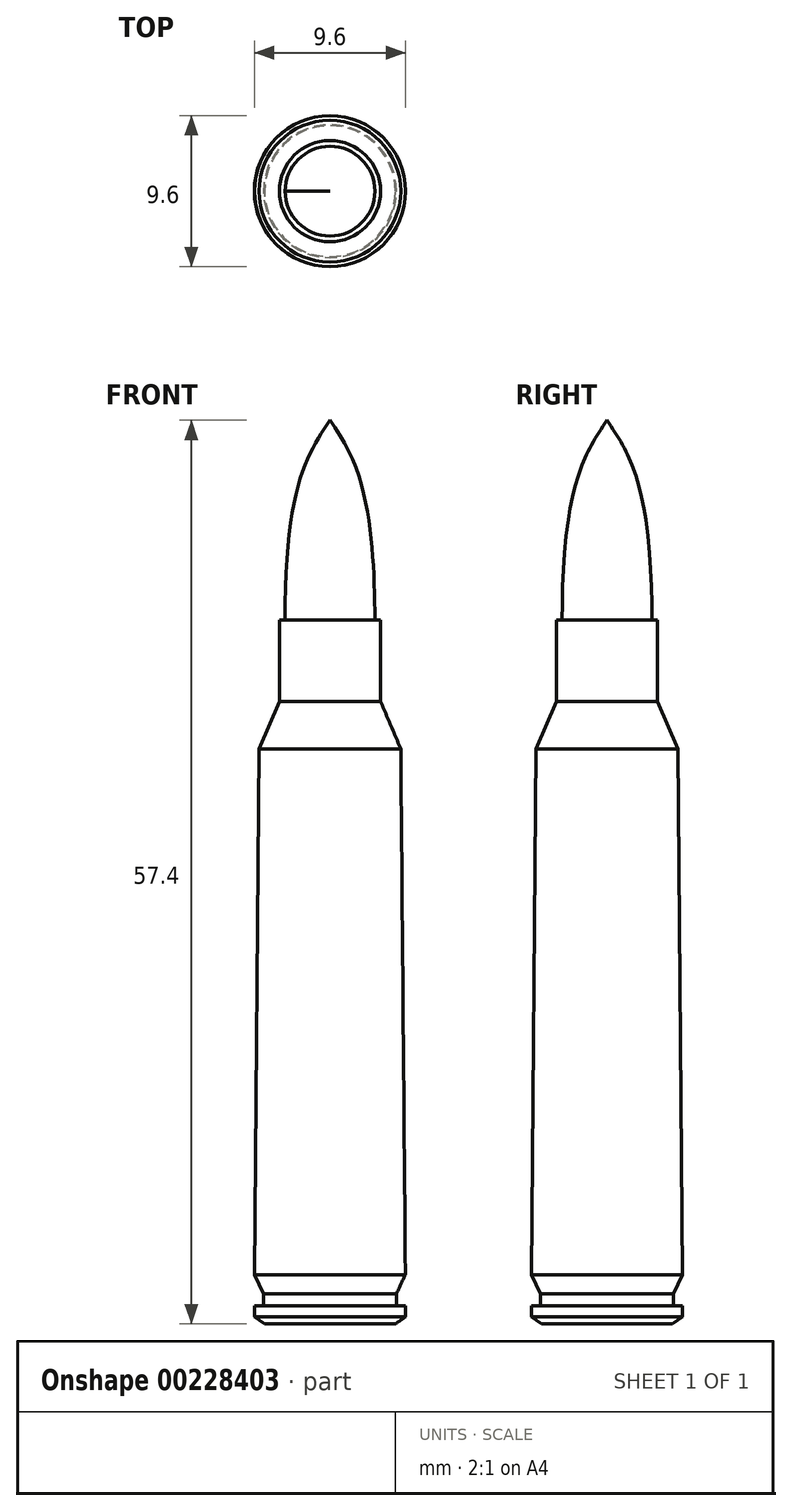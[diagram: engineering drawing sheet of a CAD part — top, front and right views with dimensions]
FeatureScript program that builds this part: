
annotation { "Feature Type Name" : "Feature", "Feature Type Description" : "" }
export const myFeature = defineFeature(function(context is Context, id is Id, definition is map)
    precondition{}
    {
        {
            var Q0;
            Q0=qCreatedBy(makeId("Top.planeOp"),FACE);
            var sketch = newSketch(context, id + "F0", { "sketchPlane" : qUnion([Q0])});
            skCircle(sketch, "E0", {"center": v(0, 0) * mm, "radius": 2.85 * mm});
            skCircle(sketch, "E1", {"center": v(0, 0) * mm, "radius": 3.21 * mm});
            skSolve(sketch);
        }
        {
            var Q0;
            Q0=qCreatedBy(makeId("Top.planeOp"),FACE);
            cPlane(context, id + "F1", {"entities" : qUnion([Q0]), "cplaneType" : CPlaneType.OFFSET, "offset" : 44.7 * mm, "oppositeDirection" : true, "width" : 150 * mm, "height" : 150 * mm});
        }
        {
            var Q0;
            Q0=qCreatedBy(id+"F1.planeOp",FACE);
            cPlane(context, id + "F2", {"entities" : qUnion([Q0]), "cplaneType" : CPlaneType.OFFSET, "offset" : 57.4 * mm, "width" : 150 * mm, "height" : 150 * mm});
        }
        {
            var Q0;
            Q0=qCreatedBy(id+"F2.planeOp",FACE);
            var sketch = newSketch(context, id + "F3", { "sketchPlane" : qUnion([Q0])});
            skPoint(sketch, "E2", {"position": v(0, 0) * mm});
            skSolve(sketch);
        }
        {
            var Q0;
            Q0=makeQuery(id+"F0.imprint","IMPRINT",FACE,{"disambiguationData":[TD([[makeQuery(id+"F0.imprint","IMPRINT",EDGE,{"derivedFrom":sQuery(id+"F0.wireOp",EDGE,"E0")}),1.0]])]});
            var Q1;
            Q1=sQuery(id+"F3.wireOp",VERTEX,"E2");
            loft(context, id + "F4", {"startCondition" : LoftEndDerivativeType.NORMAL_TO_PROFILE, "startMagnitude" : 2, "sheetProfilesArray" : [{ "sheetProfileEntities" : qUnion([Q0]) }, { "sheetProfileEntities" : qUnion([Q1]) }]});
        }
        {
            var Q0;
            Q0=qCreatedBy(makeId("Top.planeOp"),FACE);
            var sketch = newSketch(context, id + "F5", { "sketchPlane" : qUnion([Q0])});
            skCircle(sketch, "E3", {"center": v(0, 0) * mm, "radius": 3.21 * mm});
            skSolve(sketch);
        }
        {
            var Q0;
            Q0=qCreatedBy(id+"F1.planeOp",FACE);
            cPlane(context, id + "F6", {"entities" : qUnion([Q0]), "cplaneType" : CPlaneType.OFFSET, "offset" : 39.55 * mm, "width" : 150 * mm, "height" : 150 * mm});
        }
        {
            var Q0;
            Q0=qCreatedBy(id+"F6.planeOp",FACE);
            var sketch = newSketch(context, id + "F7", { "sketchPlane" : qUnion([Q0])});
            skCircle(sketch, "E4", {"center": v(0, 0) * mm, "radius": 3.21 * mm});
            skSolve(sketch);
        }
        {
            var Q1;
            Q1=makeQuery(id+"F7.imprint","IMPRINT",FACE,{"disambiguationData":[TD([[makeQuery(id+"F7.imprint","IMPRINT",EDGE,{"derivedFrom":sQuery(id+"F7.wireOp",EDGE,"E4")}),1.0]])]});
            var Q2;
            Q2=makeQuery(id+"F5.imprint","IMPRINT",FACE,{"disambiguationData":[TD([[makeQuery(id+"F5.imprint","IMPRINT",EDGE,{"derivedFrom":sQuery(id+"F5.wireOp",EDGE,"E3")}),1.0]])]});
            loft(context, id + "F8", {"operationType" : NewBodyOperationType.ADD, "sheetProfilesArray" : [{ "sheetProfileEntities" : qUnion([Q1]) }, { "sheetProfileEntities" : qUnion([Q2]) }]});
        }
        {
            var Q0;
            Q0=qCreatedBy(id+"F1.planeOp",FACE);
            cPlane(context, id + "F9", {"entities" : qUnion([Q0]), "cplaneType" : CPlaneType.OFFSET, "offset" : 36.52 * mm, "width" : 150 * mm, "height" : 150 * mm});
        }
        {
            var Q0;
            Q0=qCreatedBy(id+"F9.planeOp",FACE);
            var sketch = newSketch(context, id + "F10", { "sketchPlane" : qUnion([Q0])});
            skCircle(sketch, "E5", {"center": v(0, 0) * mm, "radius": 4.5 * mm});
            skSolve(sketch);
        }
        {
            var Q1;
            Q1=makeQuery(id+"F8.opLoft","CAP_FACE",FACE,{"disambiguationData":[OSD([makeQuery(id+"F7.imprint","IMPRINT",FACE,{"disambiguationData":[TD([[makeQuery(id+"F7.imprint","IMPRINT",EDGE,{"derivedFrom":sQuery(id+"F7.wireOp",EDGE,"E4")}),1.0]])]})])],"isStart":true});
            var Q2;
            Q2=makeQuery(id+"F10.imprint","IMPRINT",FACE,{"disambiguationData":[TD([[makeQuery(id+"F10.imprint","IMPRINT",EDGE,{"derivedFrom":sQuery(id+"F10.wireOp",EDGE,"E5")}),1.0]])]});
            loft(context, id + "F11", {"operationType" : NewBodyOperationType.ADD, "sheetProfilesArray" : [{ "sheetProfileEntities" : qUnion([Q1]) }, { "sheetProfileEntities" : qUnion([Q2]) }]});
        }
        {
            var Q0;
            Q0=qCreatedBy(id+"F1.planeOp",FACE);
            cPlane(context, id + "F12", {"entities" : qUnion([Q0]), "cplaneType" : CPlaneType.OFFSET, "offset" : 3.13 * mm, "width" : 150 * mm, "height" : 150 * mm});
        }
        {
            var Q0;
            Q0=qCreatedBy(id+"F12.planeOp",FACE);
            var sketch = newSketch(context, id + "F13", { "sketchPlane" : qUnion([Q0])});
            skCircle(sketch, "E6", {"center": v(0, 0) * mm, "radius": 4.8 * mm});
            skSolve(sketch);
        }
        {
            var Q1;
            Q1=makeQuery(id+"F11.opLoft","CAP_FACE",FACE,{"disambiguationData":[OSD([makeQuery(id+"F10.imprint","IMPRINT",FACE,{"disambiguationData":[TD([[makeQuery(id+"F10.imprint","IMPRINT",EDGE,{"derivedFrom":sQuery(id+"F10.wireOp",EDGE,"E5")}),1.0]])]})])],"isStart":true});
            var Q2;
            Q2=makeQuery(id+"F13.imprint","IMPRINT",FACE,{"disambiguationData":[TD([[makeQuery(id+"F13.imprint","IMPRINT",EDGE,{"derivedFrom":sQuery(id+"F13.wireOp",EDGE,"E6")}),1.0]])]});
            loft(context, id + "F14", {"operationType" : NewBodyOperationType.ADD, "sheetProfilesArray" : [{ "sheetProfileEntities" : qUnion([Q1]) }, { "sheetProfileEntities" : qUnion([Q2]) }]});
        }
        {
            var Q0;
            Q0=qCreatedBy(id+"F1.planeOp",FACE);
            cPlane(context, id + "F15", {"entities" : qUnion([Q0]), "cplaneType" : CPlaneType.OFFSET, "offset" : 1.9 * mm, "width" : 150 * mm, "height" : 150 * mm});
        }
        {
            var Q0;
            Q0=qCreatedBy(id+"F15.planeOp",FACE);
            var sketch = newSketch(context, id + "F16", { "sketchPlane" : qUnion([Q0])});
            skCircle(sketch, "E7", {"center": v(0, 0) * mm, "radius": 4.21 * mm});
            skSolve(sketch);
        }
        {
            var Q1;
            Q1=makeQuery(id+"F16.imprint","IMPRINT",FACE,{"disambiguationData":[TD([[makeQuery(id+"F16.imprint","IMPRINT",EDGE,{"derivedFrom":sQuery(id+"F16.wireOp",EDGE,"E7")}),1.0]])]});
            var Q2;
            Q2=makeQuery(id+"F14.opLoft","CAP_FACE",FACE,{"disambiguationData":[OSD([makeQuery(id+"F13.imprint","IMPRINT",FACE,{"disambiguationData":[TD([[makeQuery(id+"F13.imprint","IMPRINT",EDGE,{"derivedFrom":sQuery(id+"F13.wireOp",EDGE,"E6")}),1.0]])]})])],"isStart":true});
            loft(context, id + "F17", {"operationType" : NewBodyOperationType.ADD, "sheetProfilesArray" : [{ "sheetProfileEntities" : qUnion([Q1]) }, { "sheetProfileEntities" : qUnion([Q2]) }]});
        }
        {
            var Q0;
            Q0=makeQuery(id+"F17.opLoft","CAP_FACE",FACE,{"disambiguationData":[OSD([makeQuery(id+"F16.imprint","IMPRINT",FACE,{"disambiguationData":[TD([[makeQuery(id+"F16.imprint","IMPRINT",EDGE,{"derivedFrom":sQuery(id+"F16.wireOp",EDGE,"E7")}),1.0]])]})])],"isStart":true});
            extrude(context, id + "F18", {"entities" : qUnion([Q0]), "operationType" : NewBodyOperationType.ADD, "depth" : 0.76 * mm});
        }
        {
            var Q0;
            Q0=qCreatedBy(id+"F1.planeOp",FACE);
            cPlane(context, id + "F19", {"entities" : qUnion([Q0]), "cplaneType" : CPlaneType.OFFSET, "offset" : 1.14 * mm, "width" : 150 * mm, "height" : 150 * mm});
        }
        {
            var Q0;
            Q0=qCreatedBy(id+"F19.planeOp",FACE);
            var sketch = newSketch(context, id + "F20", { "sketchPlane" : qUnion([Q0])});
            skCircle(sketch, "E8", {"center": v(0, 0) * mm, "radius": 4.8 * mm});
            skSolve(sketch);
        }
        {
            var Q0;
            Q0 = qSketchRegion(id + "F20", true);
            extrude(context, id + "F21", {"entities" : qUnion([Q0]), "operationType" : NewBodyOperationType.ADD, "oppositeDirection" : true, "depth" : 0.69 * mm});
        }
        {
            var Q0;
            Q0=qCreatedBy(id+"F1.planeOp",FACE);
            var sketch = newSketch(context, id + "F22", { "sketchPlane" : qUnion([Q0])});
            skCircle(sketch, "E9", {"center": v(0, 0) * mm, "radius": 4.16 * mm});
            skSolve(sketch);
        }
        {
            var Q1;
            Q1=makeQuery(id+"F21.opExtrude","CAP_FACE",FACE,{"disambiguationData":[OSD([sQuery(id+"F20.wireOp",EDGE,"E8")])],"isStart":false});
            var Q2;
            Q2=makeQuery(id+"F22.imprint","IMPRINT",FACE,{"disambiguationData":[TD([[makeQuery(id+"F22.imprint","IMPRINT",EDGE,{"derivedFrom":sQuery(id+"F22.wireOp",EDGE,"E9")}),1.0]])]});
            loft(context, id + "F23", {"operationType" : NewBodyOperationType.ADD, "sheetProfilesArray" : [{ "sheetProfileEntities" : qUnion([Q1]) }, { "sheetProfileEntities" : qUnion([Q2]) }]});
        }
    });
